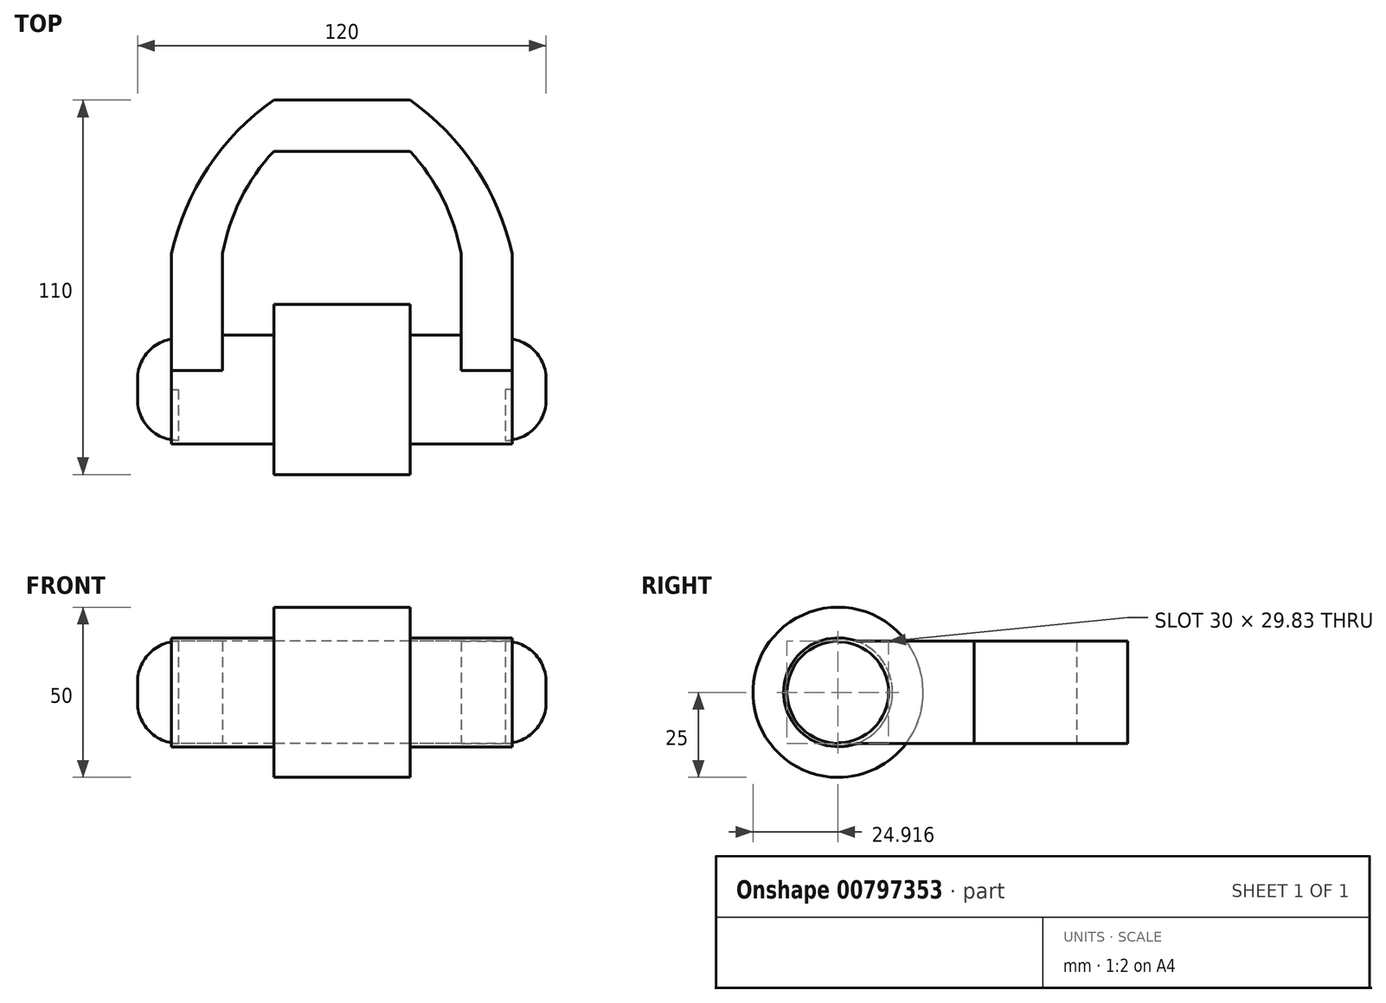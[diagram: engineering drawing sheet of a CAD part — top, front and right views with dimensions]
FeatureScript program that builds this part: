
annotation { "Feature Type Name" : "Feature", "Feature Type Description" : "" }
export const myFeature = defineFeature(function(context is Context, id is Id, definition is map)
    precondition{}
    {
        {
            var Q0;
            Q0=qCreatedBy(makeId("Top.planeOp"),FACE);
            var sketch = newSketch(context, id + "F0", { "sketchPlane" : qUnion([Q0])});
            skLineSegment(sketch, "E0", {"start": v(0, 0) * mm, "end": v(50, 0) * mm});
            skLineSegment(sketch, "E1", {"start": v(50, 0) * mm, "end": v(35, 0) * mm});
            skLineSegment(sketch, "E2", {"start": v(35, 0) * mm, "end": v(35, 40) * mm});
            skLineSegment(sketch, "E3", {"start": v(35, 40) * mm, "end": v(50, 40) * mm});
            skLineSegment(sketch, "E4", {"start": v(50, 40) * mm, "end": v(50, 0) * mm});
            skLineSegment(sketch, "E5", {"start": v(50, 0) * mm, "end": v(50, 40) * mm});
            skLineSegment(sketch, "E6", {"start": v(0, 0) * mm, "end": v(0, 85) * mm});
            skLineSegment(sketch, "E7", {"start": v(0, 85) * mm, "end": v(0, 70) * mm});
            skLineSegment(sketch, "E8", {"start": v(0, 70) * mm, "end": v(20, 70) * mm});
            skLineSegment(sketch, "E9", {"start": v(20, 70) * mm, "end": v(20, 85) * mm});
            skLineSegment(sketch, "E10", {"start": v(20, 85) * mm, "end": v(0, 85) * mm});
            skLineSegment(sketch, "E11", {"start": v(50, 40) * mm, "end": v(35, 40) * mm});
            skArc(sketch, "E12", {"start": v(50, 40) * mm, "mid": v(39.2, 65.3) * mm, "end": v(20, 85) * mm});
            skArc(sketch, "E13", {"start": v(35, 40) * mm, "mid": v(29.64, 56.07) * mm, "end": v(20, 70) * mm});
            skLineSegment(sketch, "E14.MirrorCS", {"start": v(-20, 85) * mm, "end": v(0, 85) * mm});
            skLineSegment(sketch, "E15.MirrorCS", {"start": v(0, 70) * mm, "end": v(-20, 70) * mm});
            skLineSegment(sketch, "E16.MirrorCS", {"start": v(-20, 70) * mm, "end": v(-20, 85) * mm});
            skArc(sketch, "E17.MirrorCS", {"start": v(-50, 40) * mm, "mid": v(-39.2, 65.3) * mm, "end": v(-20, 85) * mm});
            skArc(sketch, "E18.MirrorCS", {"start": v(-35, 40) * mm, "mid": v(-29.64, 56.07) * mm, "end": v(-20, 70) * mm});
            skLineSegment(sketch, "E19.MirrorCS", {"start": v(-50, 40) * mm, "end": v(-35, 40) * mm});
            skLineSegment(sketch, "E20.MirrorCS", {"start": v(-50, 40) * mm, "end": v(-50, 0) * mm});
            skLineSegment(sketch, "E21.MirrorCS", {"start": v(-35, 0) * mm, "end": v(-35, 40) * mm});
            skLineSegment(sketch, "E22.MirrorCS", {"start": v(-50, 0) * mm, "end": v(-35, 0) * mm});
            skLineSegment(sketch, "E23.MirrorCS", {"start": v(0, 0) * mm, "end": v(-50, 0) * mm});
            skSolve(sketch);
        }
        {
            var Q0;
            Q0=makeQuery(id+"F0.imprint","IMPRINT",FACE,{"disambiguationData":[TD([[makeQuery(id+"F0.imprint","IMPRINT",EDGE,{"derivedFrom":sQuery(id+"F0.wireOp",EDGE,"E19.MirrorCS")}),-1.0]])]});
            var Q1;
            Q1=makeQuery(id+"F0.imprint","IMPRINT",FACE,{"disambiguationData":[TD([[makeQuery(id+"F0.imprint","IMPRINT",EDGE,{"derivedFrom":sQuery(id+"F0.wireOp",EDGE,"E16.MirrorCS")}),1.0]])]});
            var Q2;
            {var subQ2=sQuery(id+"F0.wireOp",EDGE,"E14.MirrorCS");Q2=makeQuery(id+"F0.imprint","IMPRINT",FACE,{"disambiguationData":[TD([[makeQuery(id+"F0.imprint","IMPRINT",EDGE,{"derivedFrom":subQ2}),-1.0]])]});}
            var Q3;
            {var subQ0=sQuery(id+"F0.wireOp",EDGE,"E8");Q3=makeQuery(id+"F0.imprint","IMPRINT",FACE,{"disambiguationData":[TD([[makeQuery(id+"F0.imprint","IMPRINT",EDGE,{"derivedFrom":subQ0}),1.0]])]});}
            var Q4;
            Q4=makeQuery(id+"F0.imprint","IMPRINT",FACE,{"disambiguationData":[TD([[makeQuery(id+"F0.imprint","IMPRINT",EDGE,{"derivedFrom":sQuery(id+"F0.wireOp",EDGE,"E9")}),-1.0]])]});
            var Q5;
            Q5=makeQuery(id+"F0.imprint","IMPRINT",FACE,{"disambiguationData":[TD([[makeQuery(id+"F0.imprint","IMPRINT",EDGE,{"derivedFrom":sQuery(id+"F0.wireOp",EDGE,"E1")}),-1.0]])]});
            extrude(context, id + "F1", {"entities" : qUnion([Q0, Q1, Q2, Q3, Q4, Q5]), "depth" : 30 * mm, "offsetDistance" : 25 * mm});
        }
        {
            var Q0;
            Q0=qCreatedBy(makeId("Right.planeOp"),FACE);
            var sketch = newSketch(context, id + "F2", { "sketchPlane" : qUnion([Q0])});
            skCircle(sketch, "E24", {"center": v(0, 15) * mm, "radius": 25 * mm});
            skCircle(sketch, "E25", {"center": v(0, 15) * mm, "radius": 15 * mm});
            skSolve(sketch);
        }
        {
            var Q0;
            Q0=makeQuery(id+"F2.imprint","IMPRINT",FACE,{"disambiguationData":[TD([[makeQuery(id+"F2.imprint","IMPRINT",EDGE,{"derivedFrom":sQuery(id+"F2.wireOp",EDGE,"E24")}),1.0]])]});
            extrude(context, id + "F3", {"entities" : qUnion([Q0]), "depth" : 20 * mm, "offsetDistance" : 25 * mm, "hasSecondDirection" : true, "secondDirectionOppositeDirection" : true, "secondDirectionDepth" : 20 * mm});
        }
        {
            var Q0;
            Q0=makeQuery(id+"F2.imprint","IMPRINT",FACE,{"disambiguationData":[TD([[makeQuery(id+"F2.imprint","IMPRINT",EDGE,{"derivedFrom":sQuery(id+"F2.wireOp",EDGE,"E25")}),1.0]])]});
            extrude(context, id + "F4", {"entities" : qUnion([Q0]), "depth" : 60 * mm, "offsetDistance" : 25 * mm, "hasSecondDirection" : true, "secondDirectionOppositeDirection" : true, "secondDirectionDepth" : 60 * mm});
        }
        {
            var Q0;
            Q0=makeQuery(id+"F4.opExtrude","CAP_FACE",FACE,{"disambiguationData":[OSD([sQuery(id+"F2.wireOp",EDGE,"E25")])],"isStart":true});
            var Q1;
            Q1=makeQuery(id+"F4.opExtrude","CAP_FACE",FACE,{"disambiguationData":[OSD([sQuery(id+"F2.wireOp",EDGE,"E25")])],"isStart":false});
            fillet(context, id + "F5", {"entities" : qUnion([Q0, Q1]), "radius" : 12 * mm, "tangentPropagation" : true, "allowEdgeOverflow" : false});
        }
        {
            var Q0;
            Q0=makeQuery(id+"F1.opExtrude","SWEPT_FACE",FACE,{"disambiguationData":[OSD([sQuery(id+"F0.wireOp",EDGE,"E20.MirrorCS")])]});
            var sketch = newSketch(context, id + "F6", { "sketchPlane" : qUnion([Q0])});
            skCircle(sketch, "E26.0.0", {"center": v(0, 15) * mm, "radius": 3 * mm});
            skCircle(sketch, "E27", {"center": v(0, 15) * mm, "radius": 16 * mm});
            skCircle(sketch, "E28", {"center": v(0, 15) * mm, "radius": 15 * mm});
            skSolve(sketch);
        }
        {
            var Q0;
            {var subQ0=sQuery(id+"F6.wireOp",EDGE,"E27");var subQ1=sQuery(id+"F0.wireOp",EDGE,"E20.MirrorCS");var subQ2=makeQuery(id+"F1.opExtrude","CAP_EDGE",EDGE,{"disambiguationData":[OSD([subQ1])],"isStart":true});var subQ3=makeQuery(id+"F6.imprint","INTERSECT",VERTEX,{"derivedFrom":[subQ2,subQ0]});Q0=makeQuery(id+"F6.imprint","IMPRINT",FACE,{"disambiguationData":[TD([[makeQuery(id+"F6.imprint","IMPRINT",EDGE,{"disambiguationData":[TD([[subQ3,1.0]])],"derivedFrom":subQ0}),1.0]])]});}
            var Q1;
            {var subQ0=sQuery(id+"F6.wireOp",EDGE,"E27");var subQ1=sQuery(id+"F0.wireOp",EDGE,"E20.MirrorCS");var subQ2=makeQuery(id+"F1.opExtrude","CAP_EDGE",EDGE,{"disambiguationData":[OSD([subQ1])],"isStart":true});var subQ3=makeQuery(id+"F6.imprint","INTERSECT",VERTEX,{"derivedFrom":[subQ2,subQ0]});Q1=makeQuery(id+"F6.imprint","IMPRINT",FACE,{"disambiguationData":[TD([[makeQuery(id+"F6.imprint","IMPRINT",EDGE,{"disambiguationData":[TD([[subQ3,-1.0]])],"derivedFrom":subQ0}),1.0]])]});}
            extrude(context, id + "F7", {"entities" : qUnion([Q0, Q1]), "operationType" : NewBodyOperationType.ADD, "oppositeDirection" : true, "depth" : 30 * mm, "offsetDistance" : 25 * mm});
        }
        {
            var Q0;
            Q0=makeQuery(id+"F1.opExtrude","SWEPT_BODY",BODY,{"disambiguationData":[OSD([sQuery(id+"F0.wireOp",EDGE,"E1"),sQuery(id+"F0.wireOp",EDGE,"E2"),sQuery(id+"F0.wireOp",EDGE,"E8"),sQuery(id+"F0.wireOp",EDGE,"E10"),sQuery(id+"F0.wireOp",EDGE,"E4"),sQuery(id+"F0.wireOp",EDGE,"E12"),sQuery(id+"F0.wireOp",EDGE,"E13"),sQuery(id+"F0.wireOp",EDGE,"E14.MirrorCS"),sQuery(id+"F0.wireOp",EDGE,"E15.MirrorCS"),sQuery(id+"F0.wireOp",EDGE,"E17.MirrorCS"),sQuery(id+"F0.wireOp",EDGE,"E18.MirrorCS"),sQuery(id+"F0.wireOp",EDGE,"E20.MirrorCS"),sQuery(id+"F0.wireOp",EDGE,"E21.MirrorCS"),sQuery(id+"F0.wireOp",EDGE,"E23.MirrorCS")])]});
            var Q1;
            Q1=qCreatedBy(makeId("Right.planeOp"),FACE);
            mirror(context, id + "F8", {"operationType" : NewBodyOperationType.ADD, "entities" : qUnion([Q0]), "mirrorPlane" : qUnion([Q1])});
        }
    });
